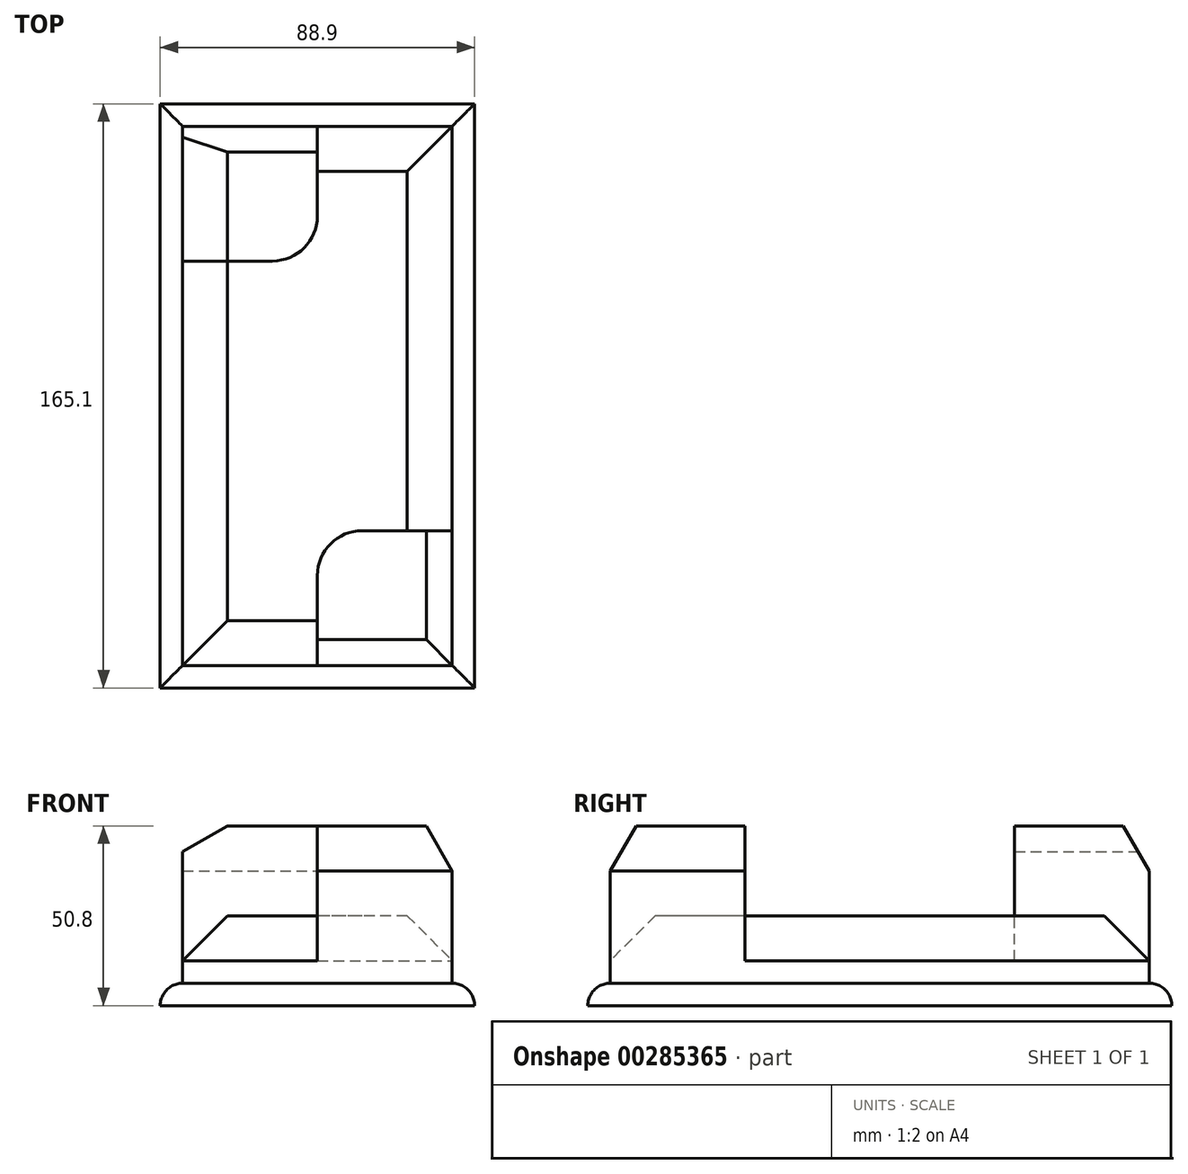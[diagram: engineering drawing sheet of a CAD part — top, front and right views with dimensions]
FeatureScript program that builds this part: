
annotation { "Feature Type Name" : "Feature", "Feature Type Description" : "" }
export const myFeature = defineFeature(function(context is Context, id is Id, definition is map)
    precondition{}
    {
        {
            var Q0;
            Q0=qCreatedBy(makeId("Top.planeOp"),FACE);
            var sketch = newSketch(context, id + "F0", { "sketchPlane" : qUnion([Q0])});
            skLineSegment(sketch, "E0.bottom", {"start": v(15.3, 106.38) * mm, "end": v(104.2, 106.38) * mm});
            skLineSegment(sketch, "E0.top", {"start": v(15.3, -58.72) * mm, "end": v(104.2, -58.72) * mm});
            skLineSegment(sketch, "E0.left", {"start": v(15.3, 106.38) * mm, "end": v(15.3, -58.72) * mm});
            skLineSegment(sketch, "E0.right", {"start": v(104.2, 106.38) * mm, "end": v(104.2, -58.72) * mm});
            skLineSegment(sketch, "E1.bottom", {"start": v(21.65, 100.03) * mm, "end": v(97.85, 100.03) * mm});
            skLineSegment(sketch, "E1.top", {"start": v(21.65, -52.37) * mm, "end": v(97.85, -52.37) * mm});
            skLineSegment(sketch, "E1.left", {"start": v(21.65, 100.03) * mm, "end": v(21.65, -52.37) * mm});
            skLineSegment(sketch, "E1.right", {"start": v(97.85, 100.03) * mm, "end": v(97.85, -52.37) * mm});
            skLineSegment(sketch, "E2", {"start": v(59.75, 100.03) * mm, "end": v(59.75, 74.63) * mm});
            skLineSegment(sketch, "E3", {"start": v(47.05, 61.93) * mm, "end": v(21.65, 61.93) * mm});
            skLineSegment(sketch, "E4", {"start": v(97.85, -14.27) * mm, "end": v(72.45, -14.27) * mm});
            skLineSegment(sketch, "E5", {"start": v(59.75, -26.97) * mm, "end": v(59.75, -52.37) * mm});
            skArc(sketch, "E6", {"start": v(47.05, 61.93) * mm, "mid": v(56.03, 65.65) * mm, "end": v(59.75, 74.63) * mm});
            skArc(sketch, "E7", {"start": v(59.75, -26.97) * mm, "mid": v(63.47, -17.99) * mm, "end": v(72.45, -14.27) * mm});
            skSolve(sketch);
        }
        {
            var Q0;
            Q0=makeQuery(id+"F0.imprint","IMPRINT",FACE,{"disambiguationData":[TD([[makeQuery(id+"F0.imprint","IMPRINT",EDGE,{"derivedFrom":sQuery(id+"F0.wireOp",EDGE,"E0.bottom")}),-1.0]])]});
            extrude(context, id + "F1", {"entities" : qUnion([Q0]), "depth" : 6.35 * mm});
        }
        {
            var Q0;
            {var subQ9=sQuery(id+"F0.wireOp",EDGE,"E2");Q0=makeQuery(id+"F0.imprint","IMPRINT",FACE,{"disambiguationData":[TD([[makeQuery(id+"F0.imprint","IMPRINT",EDGE,{"derivedFrom":subQ9}),1.0]])]});}
            extrude(context, id + "F2", {"entities" : qUnion([Q0]), "operationType" : NewBodyOperationType.ADD, "depth" : 25.4 * mm});
        }
        {
            var Q0;
            {var subQ0=sQuery(id+"F0.wireOp",EDGE,"E2");Q0=makeQuery(id+"F0.imprint","IMPRINT",FACE,{"disambiguationData":[TD([[makeQuery(id+"F0.imprint","IMPRINT",EDGE,{"derivedFrom":subQ0}),-1.0]])]});}
            var Q1;
            {var subQ1=sQuery(id+"F0.wireOp",EDGE,"E4");Q1=makeQuery(id+"F0.imprint","IMPRINT",FACE,{"disambiguationData":[TD([[makeQuery(id+"F0.imprint","IMPRINT",EDGE,{"derivedFrom":subQ1}),1.0]])]});}
            extrude(context, id + "F3", {"entities" : qUnion([Q0, Q1]), "operationType" : NewBodyOperationType.ADD, "depth" : 50.8 * mm});
        }
        {
            var Q0;
            Q0=makeQuery(id+"F1.opExtrude","CAP_EDGE",EDGE,{"disambiguationData":[OSD([sQuery(id+"F0.wireOp",EDGE,"E0.left")])],"isStart":false});
            var Q1;
            Q1=makeQuery(id+"F1.opExtrude","CAP_EDGE",EDGE,{"disambiguationData":[OSD([sQuery(id+"F0.wireOp",EDGE,"E0.bottom")])],"isStart":false});
            var Q2;
            Q2=makeQuery(id+"F1.opExtrude","CAP_EDGE",EDGE,{"disambiguationData":[OSD([sQuery(id+"F0.wireOp",EDGE,"E0.top")])],"isStart":false});
            var Q3;
            Q3=makeQuery(id+"F1.opExtrude","CAP_EDGE",EDGE,{"disambiguationData":[OSD([sQuery(id+"F0.wireOp",EDGE,"E0.right")])],"isStart":false});
            fillet(context, id + "F4", {"entities" : qUnion([Q0, Q1, Q2, Q3]), "radius" : 6.35 * mm, "tangentPropagation" : true, "allowEdgeOverflow" : false});
        }
        {
            var Q0;
            Q0=makeQuery(id+"F2.opExtrude","CAP_EDGE",EDGE,{"disambiguationData":[OSD([sQuery(id+"F0.wireOp",EDGE,"E1.left")])],"isStart":false});
            var Q1;
            Q1=makeQuery(id+"F2.opExtrude","CAP_EDGE",EDGE,{"disambiguationData":[OSD([sQuery(id+"F0.wireOp",EDGE,"E1.top")])],"isStart":false});
            var Q2;
            Q2=makeQuery(id+"F2.opExtrude","CAP_EDGE",EDGE,{"disambiguationData":[OSD([sQuery(id+"F0.wireOp",EDGE,"E1.right")])],"isStart":false});
            var Q3;
            Q3=makeQuery(id+"F2.opExtrude","CAP_EDGE",EDGE,{"disambiguationData":[OSD([sQuery(id+"F0.wireOp",EDGE,"E1.bottom")])],"isStart":false});
            chamfer(context, id + "F5", {"entities" : qUnion([Q0, Q1, Q2, Q3]), "chamferType" : ChamferType.OFFSET_ANGLE, "width" : 12.7 * mm, "oppositeDirection" : false, "angle" : 45 * degree, "tangentPropagation" : true});
        }
        {
            var Q0;
            Q0=makeQuery(id+"F3.opExtrude","CAP_EDGE",EDGE,{"disambiguationData":[OSD([sQuery(id+"F0.wireOp",EDGE,"E1.right")])],"isStart":false});
            var Q1;
            Q1=makeQuery(id+"F3.opExtrude","CAP_EDGE",EDGE,{"disambiguationData":[OSD([sQuery(id+"F0.wireOp",EDGE,"E1.top")])],"isStart":false});
            var Q2;
            Q2=makeQuery(id+"F3.opExtrude","CAP_EDGE",EDGE,{"disambiguationData":[OSD([sQuery(id+"F0.wireOp",EDGE,"E1.left")])],"isStart":false});
            var Q3;
            Q3=makeQuery(id+"F3.opExtrude","CAP_EDGE",EDGE,{"disambiguationData":[OSD([sQuery(id+"F0.wireOp",EDGE,"E1.bottom")])],"isStart":false});
            chamfer(context, id + "F6", {"entities" : qUnion([Q0, Q1, Q2, Q3]), "chamferType" : ChamferType.OFFSET_ANGLE, "width" : 12.7 * mm, "oppositeDirection" : false, "angle" : 30 * degree, "tangentPropagation" : true});
        }
    });
